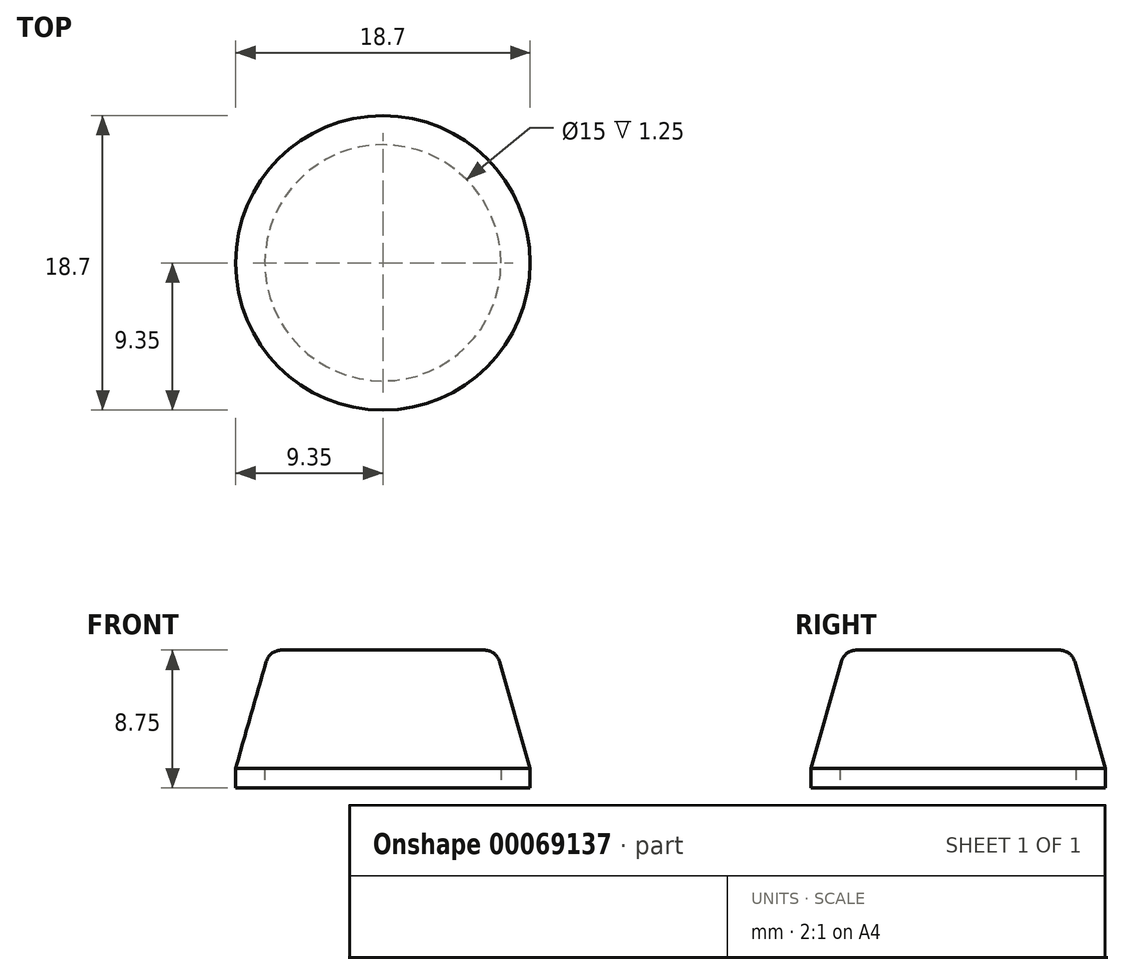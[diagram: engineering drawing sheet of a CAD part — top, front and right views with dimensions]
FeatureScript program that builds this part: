
annotation { "Feature Type Name" : "Feature", "Feature Type Description" : "" }
export const myFeature = defineFeature(function(context is Context, id is Id, definition is map)
    precondition{}
    {
        {
            var Q0;
            Q0=qCreatedBy(makeId("Front.planeOp"),FACE);
            var sketch = newSketch(context, id + "F0", { "sketchPlane" : qUnion([Q0])});
            skLineSegment(sketch, "E0", {"start": v(0, 8.75) * mm, "end": v(6.45, 8.75) * mm});
            skLineSegment(sketch, "E1", {"start": v(7.4, 8.03) * mm, "end": v(9.35, 1.25) * mm});
            skLineSegment(sketch, "E2", {"start": v(9.35, 1.25) * mm, "end": v(9.35, 0) * mm});
            skLineSegment(sketch, "E3", {"start": v(9.35, 0) * mm, "end": v(7.5, 0) * mm});
            skLineSegment(sketch, "E4", {"start": v(7.5, 0) * mm, "end": v(7.5, 1.25) * mm});
            skLineSegment(sketch, "E5", {"start": v(7.5, 1.25) * mm, "end": v(0, 1.25) * mm});
            skLineSegment(sketch, "E6", {"start": v(0, 1.25) * mm, "end": v(0, 8.75) * mm});
            skPoint(sketch, "E7.visualSharp", {"position": v(7.2, 8.75) * mm});
            skArc(sketch, "E7.filletArc", {"start": v(7.4, 8.03) * mm, "mid": v(7.05, 8.55) * mm, "end": v(6.45, 8.75) * mm});
            skSolve(sketch);
        }
        {
            var Q0;
            Q0=makeQuery(id+"F0.imprint","IMPRINT",FACE,{"disambiguationData":[TD([[makeQuery(id+"F0.imprint","IMPRINT",EDGE,{"derivedFrom":sQuery(id+"F0.wireOp",EDGE,"E0")}),-1.0]])]});
            var Q1;
            Q1=sQuery(id+"F0.wireOp",EDGE,"E6");
            revolve(context, id + "F1", {"entities" : qUnion([Q0]), "axis" : qUnion([Q1]), "revolveType" : RevolveType.FULL});
        }
    });
